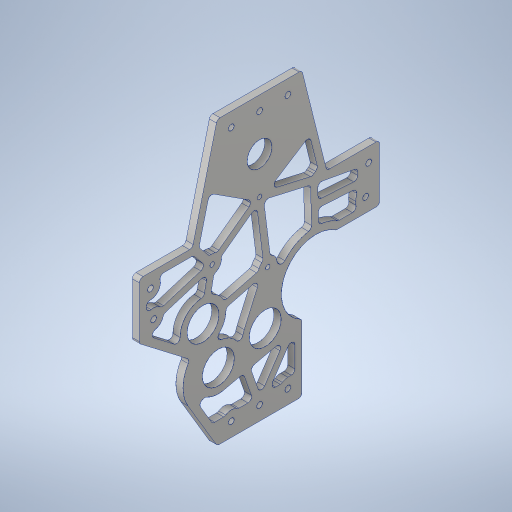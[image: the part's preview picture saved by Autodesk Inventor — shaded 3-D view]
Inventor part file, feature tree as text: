
AUTODESK INVENTOR PART (.ipt)
format: ipt  version: 2023.4 (Build 274418000, 418)  size: 854,528 bytes
history: native  units: in
note: dims shown in document units (in); Inventor stores cm internally (conversion verified against a paired STEP export)
features: sketch x6, hole x4, projected_geometry x3, extrude x2, fillet x2
ambient origin geometry x8: Origin, YZ Plane, XZ Plane, XY Plane, X Axis, Y Axis, Z Axis, Center Point
bodies: Solid1 (feature_tree)
feature tree (17):
  sketch  "Sketch1"  dims[d0=10.0in d1=1.0in]
  sketch  "Sketch2"  dims[d2=3.25in d3=1.0in]
  extrude  "Extrusion1"  Depth=10.0in
  hole  "Mount Holes"  [1 undecoded]
  hole  "Hole4"  [1 undecoded]
  hole  "Hole5"  [1 undecoded]
  hole  "Hole6"  [1 undecoded]
  extrude  "Extrusion5"  Depth=0.13in
  fillet  "Fillet5"  Radius=2.5in
  fillet  "Fillet6"  Radius=1.2in
  sketch  "Sketch7"  dims[d4=1.942in d6=3.5in]
  sketch  "Sketch8"  dims[d7=0.123in d8=1.0in]
  sketch  "Sketch9"  dims[d9=1.0in d10=0.6in]
  sketch  "Sketch10"  dims[d11=3.3in d12=0.9in d13=2.5in d14=1.2in d15=2.2in d16=2.45in d19=2.5in d23=0.8in d24=1.125in d26=1.0in d27=1.0in d28=1.0in d29=1.0in d30=0.25in d31=0.25in d32=0.25in d33=1.375in d34=2.0in d35=2.3622in d37=360.0deg d41=0.125in d42=3.0in d44=0.25in d45=0.0in d46=0.201in d47=0.75in d48=0.385in d49=0.25in d50=0.5635in d51=1.0in d52=0.8108in d60=4.006in d63=1.25in d64=1.75in d66=1.375in d67=1.25in d68=0.875in d70=0.375in d71=1.875in d73=4.6532in d74=0.5in d75=1.432in d76=4.297in d78=0.391in d79=0.391in d137=0.5in d149=8.0944in d151=1.8013in d152=4.4272in d153=0.25in d154=4.297in d155=1.432in d175=0.156in d176=0.38in d177=0.375in d178=0.25in d179=0.5635in d180=1.0in d181=0.8108in d183=2.624in d184=0.156in d185=0.38in d186=0.375in d187=0.25in d188=0.5635in d189=1.0in d190=0.8108in d194=1.625in d197=0.375in d198=0.375in d199=1.125in d201=1.432in d202=4.297in d204=2.0in d205=4.2014in d206=1.074in d207=2.2385in d208=75.0deg d209=0.156in d210=0.38in d211=0.385in d212=0.25in d213=0.5635in d214=1.0in d215=0.8108in d216=0.25in d218=0.25in d219=0.25in d220=0.25in d221=0.25in d222=0.25in d223=0.25in d224=0.25in d225=0.25in d226=0.25in d227=0.25in d228=0.25in d229=0.25in d230=0.25in d231=0.125in d232=0.125in d233=0.125in d234=0.125in d235=0.125in d236=0.125in d237=0.125in d238=0.125in d239=0.25in d240=0.25in d241=0.125in d242=0.125in d243=0.25in d244=1.0in d245=0.0in d246=0.125in d247=0.125in d248=0.125in d249=0.25in d250=0.125in d251=0.125in d252=0.125in d253=0.125in d254=0.125in d256=0.125in d257=0.656in d258=0.656in d259=0.125in d260=0.125in d261=0.13in d262=0.13in]
  projected_geometry  "Project Cut Edges4"
  projected_geometry  "Project Cut Edges5"
  projected_geometry  "Project Cut Edges6"
note: 4 required parameter values undecoded (feature->parameter linkage not recoverable at this tier; creation-order binding heuristic only, values carry confidence <= 0.55)
